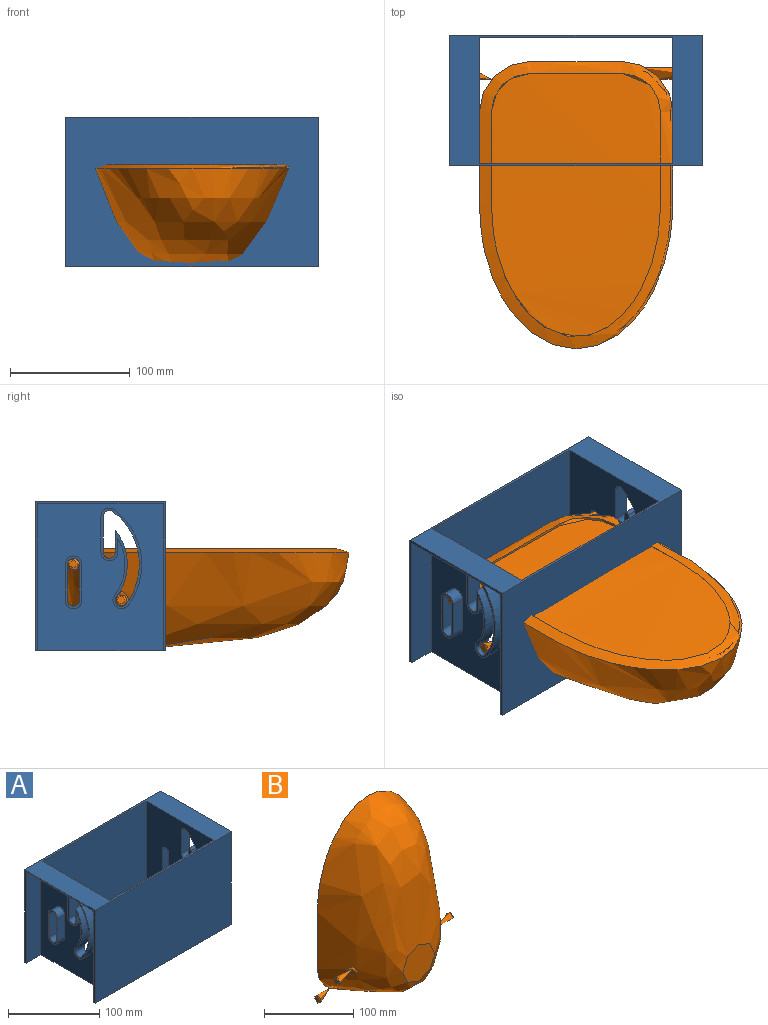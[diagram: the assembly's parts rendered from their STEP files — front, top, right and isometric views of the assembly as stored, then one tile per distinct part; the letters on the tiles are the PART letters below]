
ASSEMBLY  parts=2 mates=1
PART A: 67 faces, bbox 211.2x109x124.6 mm
  f0: plane 211.25x109mm, normal (0,0,1), area 6095mm2, adj f1,f4,f5,f17,f29,f30,f64,f65
  f1: plane 124.57x109mm, normal (1,0,0), area 708.3mm2, adj f0,f2,f30,f44,f63,f65,f66
  f2: plane 105x23mm, normal (0,0,-1), area 2415mm2, adj f1,f31,f44,f63
  f3: plane 105x23mm, normal (0,0,-1), area 2415mm2, adj f4,f58,f59,f62
  f4: plane 124.57x109mm, normal (-1,0,0), area 708.3mm2, adj f0,f3,f30,f59,f62,f65,f66
  f5: plane 124.57x105mm, normal (1,0,0), area 11563.9mm2, adj f0,f6,f7,f8,f9,f10,f11,f12
  f6: plane 30x13mm, normal (0,1,0), area 390mm2, adj f5,f7,f9,f57
  f7: cylinder r=5mm len=13mm, axis (1,0,0), area 204.2mm2, adj f5,f6,f8,f57
  f8: plane 30x13mm, normal (0,-1,0), area 390mm2, adj f5,f7,f9,f57
  f9: cylinder r=5mm len=13mm, axis (1,0,0), area 204.2mm2, adj f5,f6,f8,f57
  f10: cylinder r=5mm len=13mm, axis (1,0,0), area 204.2mm2, adj f5,f11,f16,f52
  f11: plane 30x13mm, normal (0,-1,0), area 390mm2, adj f5,f10,f12,f52
  f12: cylinder r=5mm len=13mm, axis (1,0,0), area 143.9mm2, adj f5,f11,f13,f52
  f13: cylinder r=55mm len=77mm, axis (1,0,0), area 1123.1mm2, adj f5,f12,f14,f52
  f14: cylinder r=5mm len=13mm, axis (1,0,0), area 204.2mm2, adj f5,f13,f15,f52
  f15: cylinder r=45mm len=55.28mm, axis (1,0,0), area 774.1mm2, adj f5,f14,f16,f52
  f16: plane 18.28x13mm, normal (0,1,0), area 237.7mm2, adj f5,f10,f15,f52
  f17: plane 124.57x105mm, normal (-1,0,0), area 11550.1mm2, adj f0,f18,f19,f20,f21,f22,f23,f24
  f18: plane 30x13mm, normal (0,1,0), area 390mm2, adj f17,f19,f21,f32
  f19: cylinder r=5mm len=13mm, axis (-1,0,0), area 204.2mm2, adj f17,f18,f20,f32
  f20: plane 30x13mm, normal (0,-1,0), area 390mm2, adj f17,f19,f21,f32
  f21: cylinder r=5mm len=13mm, axis (-1,0,0), area 204.2mm2, adj f17,f18,f20,f32
  f22: cylinder r=5mm len=13mm, axis (-1,0,0), area 204.2mm2, adj f17,f23,f28,f37
  f23: plane 30x13mm, normal (0,-1,0), area 390mm2, adj f17,f22,f24,f37
  f24: cylinder r=5mm len=13mm, axis (-1,0,0), area 143.9mm2, adj f17,f23,f25,f37
  f25: cylinder r=55mm len=77mm, axis (-1,0,0), area 1123.1mm2, adj f17,f24,f26,f37
  f26: cylinder r=5mm len=13mm, axis (-1,0,0), area 204.2mm2, adj f17,f25,f27,f37
  f27: cylinder r=45mm len=48.18mm, axis (-1,0,0), area 663.1mm2, adj f17,f26,f37,f61
  f28: plane 13x10mm, normal (0,1,0), area 130mm2, adj f17,f22,f37,f61
  f29: plane 161.25x124.57mm, normal (0,-1,0), area 20086.2mm2, adj f0,f5,f17,f66
  f30: plane 211.25x124.57mm, normal (0,1,0), area 26314.7mm2, adj f0,f1,f4,f66
  f31: plane 122.57x105mm, normal (1,0,0), area 10652.4mm2, adj f2,f33,f34,f35,f36,f38,f39,f40
  f32: plane 44x14mm, normal (1,0,0), area 195.4mm2, adj f18,f19,f20,f21,f33,f34,f35,f36
  f33: plane 30x11mm, normal (0,-1,0), area 330mm2, adj f31,f32,f34,f36
  f34: cylinder r=7mm len=14mm, axis (-1,0,0), area 241.9mm2, adj f31,f32,f33,f35
  f35: plane 30x11mm, normal (0,1,0), area 330mm2, adj f31,f32,f34,f36
  f36: cylinder r=7mm len=14mm, axis (-1,0,0), area 241.9mm2, adj f31,f32,f33,f35
  f37: plane 84x34mm, normal (1,0,0), area 492.3mm2, adj f22,f23,f24,f25,f26,f27,f28,f38
  f38: cylinder r=7mm len=13.97mm, axis (-1,0,0), area 234.8mm2, adj f31,f37,f39,f60
  f39: plane 30x11mm, normal (0,1,0), area 330mm2, adj f31,f37,f38,f40
  f40: cylinder r=7mm len=11.2mm, axis (-1,0,0), area 170.5mm2, adj f31,f37,f39,f41
  f41: cylinder r=57mm len=79.8mm, axis (-1,0,0), area 984.9mm2, adj f31,f37,f40,f42
  f42: cylinder r=7mm len=12.6mm, axis (-1,0,0), area 241.9mm2, adj f31,f37,f41,f43
  f43: cylinder r=43mm len=35.49mm, axis (-1,0,0), area 411.8mm2, adj f31,f37,f42,f60
  f44: plane 122.57x23mm, normal (0,-1,0), area 2819.1mm2, adj f1,f2,f31,f66
  f45: plane 11.91x11mm, normal (0,-1,0), area 131mm2, adj f46,f51,f52,f58
  f46: cylinder r=43mm len=47.71mm, axis (1,0,0), area 557.2mm2, adj f45,f47,f52,f58
  f47: cylinder r=7mm len=12.6mm, axis (1,0,0), area 241.9mm2, adj f46,f48,f52,f58
  f48: cylinder r=57mm len=79.8mm, axis (1,0,0), area 984.9mm2, adj f47,f49,f52,f58
  f49: cylinder r=7mm len=11.2mm, axis (1,0,0), area 170.5mm2, adj f48,f50,f52,f58
  f50: plane 30x11mm, normal (0,1,0), area 330mm2, adj f49,f51,f52,f58
  f51: cylinder r=7mm len=14mm, axis (1,0,0), area 241.9mm2, adj f45,f50,f52,f58
  f52: plane 84x34mm, normal (-1,0,0), area 478.8mm2, adj f10,f11,f12,f13,f14,f15,f16,f45
  f53: cylinder r=7mm len=14mm, axis (1,0,0), area 241.9mm2, adj f54,f56,f57,f58
  f54: plane 30x11mm, normal (0,1,0), area 330mm2, adj f53,f55,f57,f58
  f55: cylinder r=7mm len=14mm, axis (1,0,0), area 241.9mm2, adj f54,f56,f57,f58
  f56: plane 30x11mm, normal (0,-1,0), area 330mm2, adj f53,f55,f57,f58
  f57: plane 44x14mm, normal (-1,0,0), area 195.4mm2, adj f6,f7,f8,f9,f53,f54,f55,f56
  f58: plane 122.57x105mm, normal (-1,0,0), area 10679.8mm2, adj f3,f45,f46,f47,f48,f49,f50,f51
  f59: plane 122.57x23mm, normal (0,-1,0), area 2819.1mm2, adj f3,f4,f58,f66
  f60: cylinder r=2.5mm len=11mm, axis (-1,0,0), area 77.6mm2, adj f31,f37,f38,f43
  f61: cylinder r=2.5mm len=13mm, axis (-1,0,0), area 86.2mm2, adj f17,f27,f28,f37
  f62: plane 122.57x23mm, normal (0,1,0), area 2819.1mm2, adj f3,f4,f58,f66
  f63: plane 122.57x23mm, normal (0,1,0), area 2819.1mm2, adj f1,f2,f31,f66
  f64: plane 161.25x124.57mm, normal (0,1,0), area 20086.2mm2, adj f0,f5,f17,f66
  f65: plane 211.25x124.57mm, normal (0,-1,0), area 26314.7mm2, adj f0,f1,f4,f66
  f66: plane 211.25x109mm, normal (0,0,-1), area 1265mm2, adj f1,f4,f5,f17,f29,f30,f31,f44
PART B: 28 faces, bbox 4204.4x3995.1x30657.9 mm
  f0: bspline ~240x161.25mm, area 57808.9mm2, adj f1,f4,f20,f21,f22,f23
  f1: plane 51.29x51.29mm, normal (0,-1,0), area 1963.4mm2, adj f0
  f2: offset ~766.8x151.2mm, area 4838.6mm2, adj f3,f5,f6,f7,f9,f10
  f3: offset ~26749.72x286.93mm, area 23015.2mm2, adj f2,f8,f9,f10,f11
  f4: bspline ~240x161.65mm, area 7178.5mm2, adj f0,f5,f6,f7,f8,f9,f10
  f5: plane 78.01x2.77mm, normal (0,0,1), area 154.7mm2, adj f2,f4,f6,f9
  f6: cylinder r=32mm len=32mm, axis (0,1,0), area 100.6mm2, adj f2,f4,f5,f7
  f7: plane 81.14x5.14mm, normal (-1,0,0), area 156.2mm2, adj f2,f4,f6,f10
  f8: plane 3990.14x3914.33mm, normal (1,0,0), area 171.5mm2, adj f3,f4,f9,f10
  f9: cylinder r=32mm len=32mm, axis (0,1,0), area 102.4mm2, adj f2,f3,f4,f5,f8
  f10: extruded ~141.25x110mm, area 584.6mm2, adj f2,f3,f4,f7,f8
  f11: plane 2472.72x2392.26mm, normal (0,1,0), area 30920.9mm2, adj f3
  f12: plane 8x8mm, normal (1,0,0), area 50.3mm2, adj f27
  f13: cylinder r=5mm len=38.54mm, axis (1,0,0), area 867.7mm2, adj f23,f27
  f14: plane 8x8mm, normal (1,0,0), area 50.3mm2, adj f26
  f15: cylinder r=5mm len=27.08mm, axis (1,0,0), area 738.2mm2, adj f22,f26
  f16: cylinder r=5mm len=23.39mm, axis (-1,0,0), area 734.7mm2, adj f21,f25
  f17: plane 8x8mm, normal (-1,0,0), area 50.3mm2, adj f25
  f18: cylinder r=5mm len=38.54mm, axis (-1,0,0), area 867.6mm2, adj f20,f24
  f19: plane 8x8mm, normal (-1,0,0), area 50.3mm2, adj f24
  f20: bspline ~20.62x14.02mm, area 149.6mm2, adj f0,f18
  f21: bspline ~13.88x13.74mm, area 116.9mm2, adj f0,f16
  f22: bspline ~13.88x13.74mm, area 117mm2, adj f0,f15
  f23: bspline ~20.63x14.01mm, area 149.6mm2, adj f0,f13
  f24: torus R=4mm, axis (1,0,0), area 45.8mm2, adj f18,f19
  f25: torus R=4mm, axis (1,0,0), area 45.8mm2, adj f16,f17
  f26: torus R=4mm, axis (1,0,0), area 45.8mm2, adj f14,f15
  f27: torus R=4mm, axis (1,0,0), area 45.8mm2, adj f12,f13
PLACE A at identity fixed
PLACE B rot(axis=(1,0,0),90deg) t=(0,40,10)mm
MATE planar B.f15 <-> A.f10  axis (1,0,0) through (90.62,-10,10)mm
